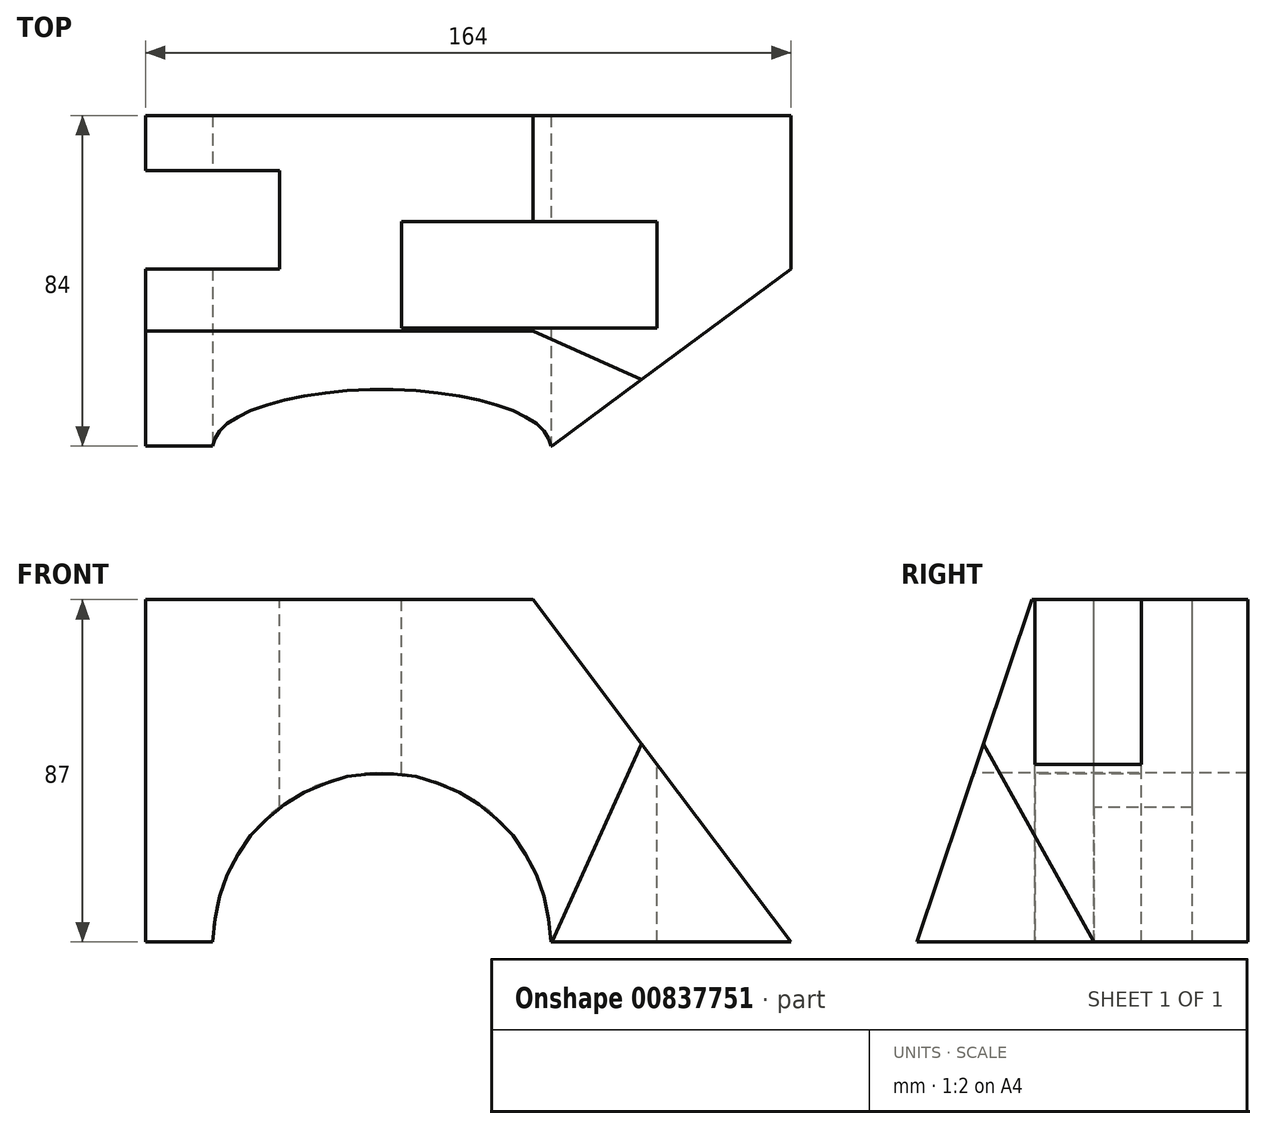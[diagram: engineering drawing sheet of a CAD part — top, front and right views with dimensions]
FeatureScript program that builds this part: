
annotation { "Feature Type Name" : "Feature", "Feature Type Description" : "" }
export const myFeature = defineFeature(function(context is Context, id is Id, definition is map)
    precondition{}
    {
        {
            var Q0;
            Q0=qCreatedBy(makeId("Front.planeOp"),FACE);
            var sketch = newSketch(context, id + "F0", { "sketchPlane" : qUnion([Q0])});
            skLineSegment(sketch, "E0", {"start": v(-72.25, 48.3) * mm, "end": v(-72.25, -38.7) * mm});
            skLineSegment(sketch, "E1", {"start": v(-72.25, -38.7) * mm, "end": v(91.75, -38.7) * mm});
            skLineSegment(sketch, "E2", {"start": v(26.2, 48.3) * mm, "end": v(-72.25, 48.3) * mm});
            skLineSegment(sketch, "E3", {"start": v(91.75, -38.7) * mm, "end": v(26.2, 48.3) * mm});
            skPoint(sketch, "E4.end.orphan", {"position": v(91.75, 48.3) * mm});
            skSolve(sketch);
        }
        {
            var Q0;
            Q0=makeQuery(id+"F0.imprint","IMPRINT",FACE,{"disambiguationData":[TD([[makeQuery(id+"F0.imprint","IMPRINT",EDGE,{"derivedFrom":sQuery(id+"F0.wireOp",EDGE,"E0")}),1.0]])]});
            extrude(context, id + "F1", {"entities" : qUnion([Q0]), "depth" : 84 * mm, "offsetDistance" : 25 * mm});
        }
        {
            var Q0;
            Q0=makeQuery(id+"F1.opExtrude","SWEPT_FACE",FACE,{"disambiguationData":[OSD([sQuery(id+"F0.wireOp",EDGE,"E2")])]});
            cPlane(context, id + "F2", {"entities" : qUnion([Q0]), "cplaneType" : CPlaneType.OFFSET, "offset" : 25 * mm, "width" : 150 * mm, "height" : 150 * mm});
        }
        {
            var Q0;
            Q0=qCreatedBy(id+"F2.planeOp",FACE);
            var sketch = newSketch(context, id + "F3", { "sketchPlane" : qUnion([Q0])});
            skLineSegment(sketch, "E5.0.0", {"start": v(26.2, 0) * mm, "end": v(-72.25, 0) * mm});
            skLineSegment(sketch, "E5.0.1", {"start": v(-72.25, 0) * mm, "end": v(-72.25, -84) * mm});
            skLineSegment(sketch, "E5.0.2", {"start": v(-72.25, -84) * mm, "end": v(26.2, -84) * mm});
            skLineSegment(sketch, "E5.0.3", {"start": v(26.2, -84) * mm, "end": v(26.2, 0) * mm});
            skLineSegment(sketch, "E6.0.0", {"start": v(91.75, 0) * mm, "end": v(26.2, 0) * mm});
            skLineSegment(sketch, "E6.0.1", {"start": v(26.2, 0) * mm, "end": v(26.2, -84) * mm});
            skLineSegment(sketch, "E6.0.2", {"start": v(26.2, -84) * mm, "end": v(91.75, -84) * mm});
            skLineSegment(sketch, "E6.0.3", {"start": v(91.75, -84) * mm, "end": v(91.75, 0) * mm});
            skLineSegment(sketch, "E7", {"start": v(91.75, 0) * mm, "end": v(57.75, 0) * mm});
            skLineSegment(sketch, "E8", {"start": v(57.75, 0) * mm, "end": v(-7.25, 0) * mm});
            skLineSegment(sketch, "E9", {"start": v(-7.25, 0) * mm, "end": v(-7.25, -27) * mm});
            skLineSegment(sketch, "E10", {"start": v(-7.25, -27) * mm, "end": v(57.75, -27) * mm});
            skLineSegment(sketch, "E11", {"start": v(57.75, -27) * mm, "end": v(57.75, 0) * mm});
            skLineSegment(sketch, "E12", {"start": v(57.75, -27) * mm, "end": v(57.75, -54) * mm});
            skLineSegment(sketch, "E13", {"start": v(57.75, -54) * mm, "end": v(-7.25, -54) * mm});
            skLineSegment(sketch, "E14", {"start": v(-7.25, -54) * mm, "end": v(-7.25, -27) * mm});
            skSolve(sketch);
        }
        {
            var Q0;
            {var subQ5=sQuery(id+"F3.wireOp",EDGE,"E14");Q0=makeQuery(id+"F3.imprint","IMPRINT",FACE,{"disambiguationData":[TD([[makeQuery(id+"F3.imprint","IMPRINT",EDGE,{"derivedFrom":subQ5}),-1.0]])]});}
            var Q1;
            {var subQ5=sQuery(id+"F3.wireOp",EDGE,"E12");Q1=makeQuery(id+"F3.imprint","IMPRINT",FACE,{"disambiguationData":[TD([[makeQuery(id+"F3.imprint","IMPRINT",EDGE,{"derivedFrom":subQ5}),-1.0]])]});}
            extrude(context, id + "F4", {"entities" : qUnion([Q0, Q1]), "operationType" : NewBodyOperationType.REMOVE, "oppositeDirection" : true, "depth" : 184 * mm, "offsetDistance" : 25 * mm});
        }
        {
            var Q0;
            Q0=makeQuery(id+"F1.opExtrude","SWEPT_FACE",FACE,{"disambiguationData":[OSD([sQuery(id+"F0.wireOp",EDGE,"E2")])]});
            var sketch = newSketch(context, id + "F5", { "sketchPlane" : qUnion([Q0])});
            skLineSegment(sketch, "E15", {"start": v(-72.25, 0) * mm, "end": v(-72.25, -14) * mm});
            skLineSegment(sketch, "E16", {"start": v(-72.25, -14) * mm, "end": v(-72.25, -39) * mm});
            skLineSegment(sketch, "E17", {"start": v(-72.25, -39) * mm, "end": v(-38.25, -39) * mm});
            skLineSegment(sketch, "E18", {"start": v(-38.25, -39) * mm, "end": v(-38.25, -14) * mm});
            skLineSegment(sketch, "E19", {"start": v(-38.25, -14) * mm, "end": v(-72.25, -14) * mm});
            skSolve(sketch);
        }
        {
            var Q0;
            Q0 = qSketchRegion(id + "F5", true);
            extrude(context, id + "F6", {"entities" : qUnion([Q0]), "operationType" : NewBodyOperationType.REMOVE, "oppositeDirection" : true, "depth" : 363 * mm, "offsetDistance" : 25 * mm});
        }
        {
            var Q0;
            Q0=makeQuery(id+"F1.opExtrude","CAP_FACE",FACE,{"disambiguationData":[OSD([sQuery(id+"F0.wireOp",EDGE,"E0"),sQuery(id+"F0.wireOp",EDGE,"E1"),sQuery(id+"F0.wireOp",EDGE,"E2"),sQuery(id+"F0.wireOp",EDGE,"E3")])],"isStart":false});
            var sketch = newSketch(context, id + "F7", { "sketchPlane" : qUnion([Q0])});
            skLineSegment(sketch, "E20", {"start": v(-72.25, -38.7) * mm, "end": v(-12.25, -38.7) * mm});
            skCircle(sketch, "E21", {"center": v(-12.25, -38.7) * mm, "radius": 43 * mm});
            skSolve(sketch);
        }
        {
            var Q0;
            Q0 = qSketchRegion(id + "F7", true);
            extrude(context, id + "F8", {"entities" : qUnion([Q0]), "operationType" : NewBodyOperationType.REMOVE, "oppositeDirection" : true, "depth" : 191 * mm, "offsetDistance" : 25 * mm});
        }
        {
            var Q0;
            Q0=makeQuery(id+"F1.opExtrude","SWEPT_FACE",FACE,{"disambiguationData":[OSD([sQuery(id+"F0.wireOp",EDGE,"E3")])]});
            var sketch = newSketch(context, id + "F9", { "sketchPlane" : qUnion([Q0])});
            skLineSegment(sketch, "E22", {"start": v(0, -86.13) * mm, "end": v(-64, -86.13) * mm});
            skSolve(sketch);
        }
        {
            var Q0;
            Q0=makeQuery(id+"F1.opExtrude","CAP_FACE",FACE,{"disambiguationData":[OSD([sQuery(id+"F0.wireOp",EDGE,"E0"),sQuery(id+"F0.wireOp",EDGE,"E1"),sQuery(id+"F0.wireOp",EDGE,"E2"),sQuery(id+"F0.wireOp",EDGE,"E3")])],"isStart":false});
            var sketch = newSketch(context, id + "F10", { "sketchPlane" : qUnion([Q0])});
            skLineSegment(sketch, "E23", {"start": v(30.75, -38.7) * mm, "end": v(80.75, -38.7) * mm});
            skSolve(sketch);
        }
        {
            var Q0;
            {var subQ4=sQuery(id+"F9.wireOp",EDGE,"E22");Q0=makeQuery(id+"F9.imprint","IMPRINT",FACE,{"disambiguationData":[TD([[makeQuery(id+"F9.imprint","IMPRINT",EDGE,{"derivedFrom":subQ4}),1.0]])]});}
            var sketch = newSketch(context, id + "F11", { "sketchPlane" : qUnion([Q0])});
            skPoint(sketch, "E24.0", {"position": v(-84, -86.13) * mm});
            skLineSegment(sketch, "E25", {"start": v(-84, -86.13) * mm, "end": v(-51.09, 36.7) * mm});
            skLineSegment(sketch, "E26.0.0", {"start": v(-54, -29.64) * mm, "end": v(-54, 22.8) * mm});
            skLineSegment(sketch, "E26.0.1", {"start": v(-54, 22.8) * mm, "end": v(-84, 22.8) * mm});
            skLineSegment(sketch, "E26.0.2", {"start": v(-84, 22.8) * mm, "end": v(-84, -86.13) * mm});
            skLineSegment(sketch, "E26.0.3", {"start": v(-84, -86.13) * mm, "end": v(-64, -86.13) * mm});
            skLineSegment(sketch, "E26.0.4", {"start": v(-64, -86.13) * mm, "end": v(0, -86.13) * mm});
            skLineSegment(sketch, "E26.0.5", {"start": v(0, -86.13) * mm, "end": v(0, 22.8) * mm});
            skLineSegment(sketch, "E26.0.6", {"start": v(0, 22.8) * mm, "end": v(-27, 22.8) * mm});
            skLineSegment(sketch, "E26.0.7", {"start": v(-27, 22.8) * mm, "end": v(-27, -29.64) * mm});
            skLineSegment(sketch, "E26.0.8", {"start": v(-27, -29.64) * mm, "end": v(-54, -29.64) * mm});
            skLineSegment(sketch, "E27.0", {"start": v(-27, 42.93) * mm, "end": v(-54, 42.93) * mm});
            skSolve(sketch);
        }
        {
            var Q0;
            Q0=qCreatedBy(makeId("Right.planeOp"),FACE);
            var sketch = newSketch(context, id + "F12", { "sketchPlane" : qUnion([Q0])});
            skLineSegment(sketch, "E28.0", {"start": v(-84, -38.7) * mm, "end": v(-51.09, 59.4) * mm});
            skLineSegment(sketch, "E29.0.0", {"start": v(-84, 48.3) * mm, "end": v(-84, -38.7) * mm});
            skLineSegment(sketch, "E29.0.1", {"start": v(-84, -38.7) * mm, "end": v(-54.81, 48.3) * mm});
            skLineSegment(sketch, "E29.0.2", {"start": v(-54.81, 48.3) * mm, "end": v(-84, 48.3) * mm});
            skPoint(sketch, "E30.0", {"position": v(-84, 4.8) * mm});
            skLineSegment(sketch, "E31.0.0", {"start": v(-84, -38.7) * mm, "end": v(-84, 4.3) * mm});
            skLineSegment(sketch, "E31.0.3", {"start": v(-84, -38.7) * mm, "end": v(-84, 48.3) * mm});
            skSolve(sketch);
        }
        {
            var Q0;
            Q0 = qSketchRegion(id + "F12", true);
            extrude(context, id + "F13", {"entities" : qUnion([Q0]), "operationType" : NewBodyOperationType.REMOVE, "oppositeDirection" : true, "depth" : 133.5 * mm, "offsetDistance" : 25 * mm, "hasSecondDirection" : true, "secondDirectionOppositeDirection" : false, "secondDirectionDepth" : 142.2 * mm});
        }
        {
            var Q0;
            Q0=qCreatedBy(makeId("Top.planeOp"),FACE);
            var sketch = newSketch(context, id + "F14", { "sketchPlane" : qUnion([Q0])});
            skLineSegment(sketch, "E32.0", {"start": v(91.75, -64) * mm, "end": v(91.75, 0) * mm});
            skLineSegment(sketch, "E33", {"start": v(91.75, 0) * mm, "end": v(91.75, -39) * mm});
            skLineSegment(sketch, "E34.0", {"start": v(26.2, -84) * mm, "end": v(91.75, -84) * mm});
            skLineSegment(sketch, "E35", {"start": v(91.75, -39) * mm, "end": v(30.99, -84) * mm});
            skLineSegment(sketch, "E36", {"start": v(30.99, -84) * mm, "end": v(91.75, -84) * mm});
            skLineSegment(sketch, "E37", {"start": v(91.75, -84) * mm, "end": v(91.75, -64) * mm});
            skSolve(sketch);
        }
        {
            var Q0;
            Q0=makeQuery(id+"F14.imprint","IMPRINT",FACE,{"disambiguationData":[TD([[makeQuery(id+"F14.imprint","IMPRINT",EDGE,{"derivedFrom":sQuery(id+"F14.wireOp",EDGE,"E32.0")}),1.0]])]});
            extrude(context, id + "F15", {"entities" : qUnion([Q0]), "operationType" : NewBodyOperationType.REMOVE, "depth" : 289 * mm, "offsetDistance" : 25 * mm, "hasSecondDirection" : true, "secondDirectionOppositeDirection" : true, "secondDirectionDepth" : 99 * mm});
        }
    });
